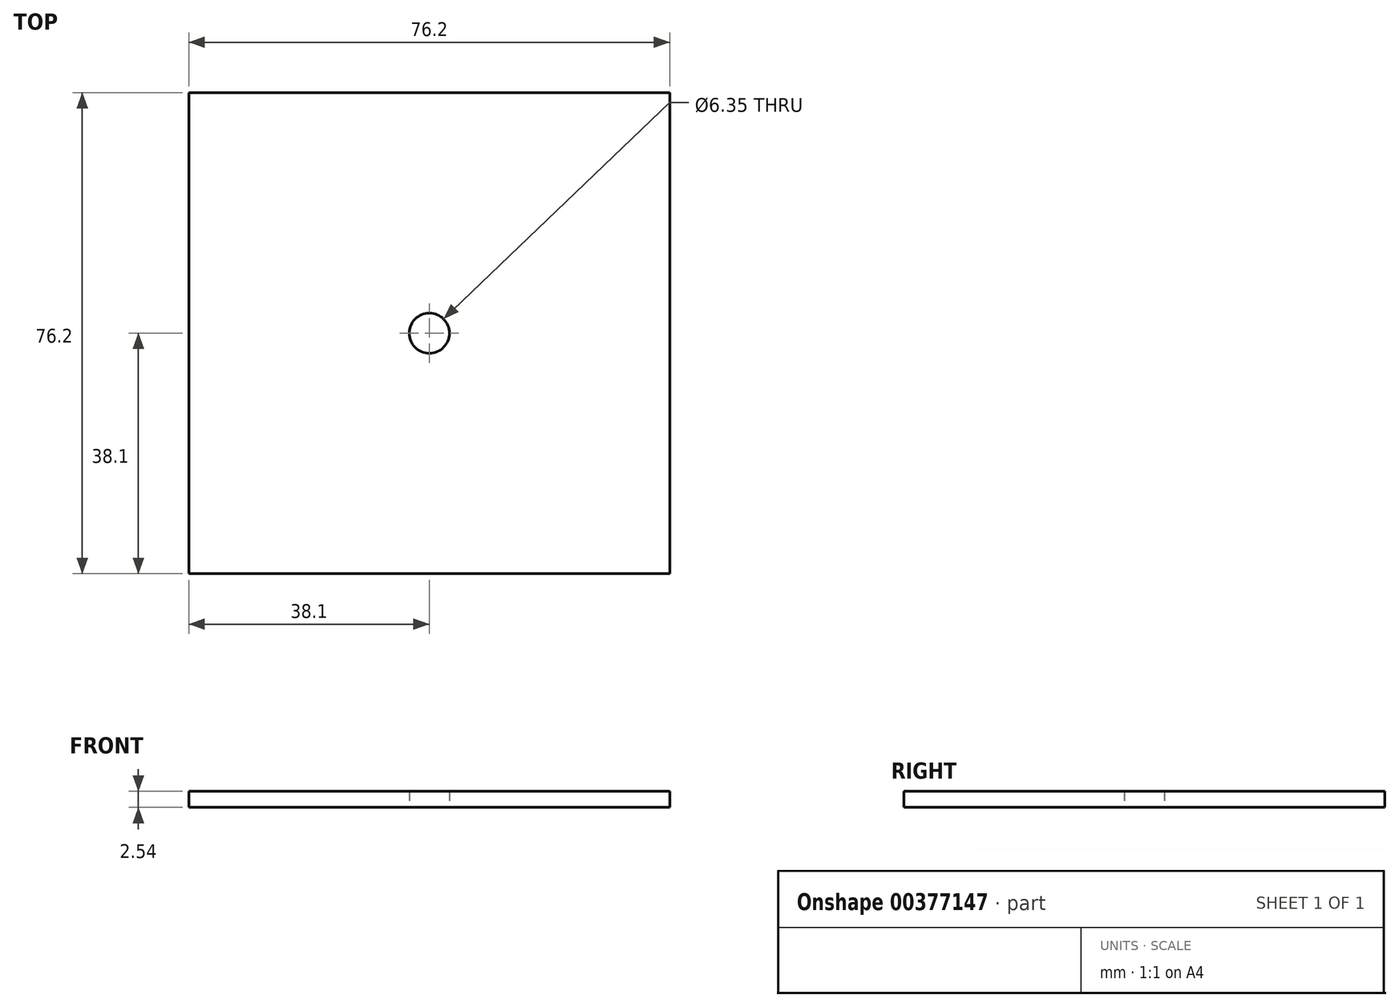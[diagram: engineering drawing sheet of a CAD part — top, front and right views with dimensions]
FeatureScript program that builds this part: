
annotation { "Feature Type Name" : "Feature", "Feature Type Description" : "" }
export const myFeature = defineFeature(function(context is Context, id is Id, definition is map)
    precondition{}
    {
        {
            var Q0;
            Q0=qCreatedBy(makeId("Top.planeOp"),FACE);
            var sketch = newSketch(context, id + "F0", { "sketchPlane" : qUnion([Q0])});
            skLineSegment(sketch, "E0.bottom", {"start": v(-38.1, 38.1) * mm, "end": v(38.1, 38.1) * mm});
            skLineSegment(sketch, "E0.top", {"start": v(-38.1, -38.1) * mm, "end": v(38.1, -38.1) * mm});
            skLineSegment(sketch, "E0.left", {"start": v(-38.1, 38.1) * mm, "end": v(-38.1, -38.1) * mm});
            skLineSegment(sketch, "E0.right", {"start": v(38.1, 38.1) * mm, "end": v(38.1, -38.1) * mm});
            skCircle(sketch, "E1", {"center": v(0, 0) * mm, "radius": 3.18 * mm});
            skSolve(sketch);
        }
        {
            var Q0;
            Q0 = qSketchRegion(id + "F0", true);
            extrude(context, id + "F1", {"entities" : qUnion([Q0]), "depth" : 2.54 * mm});
        }
    });
